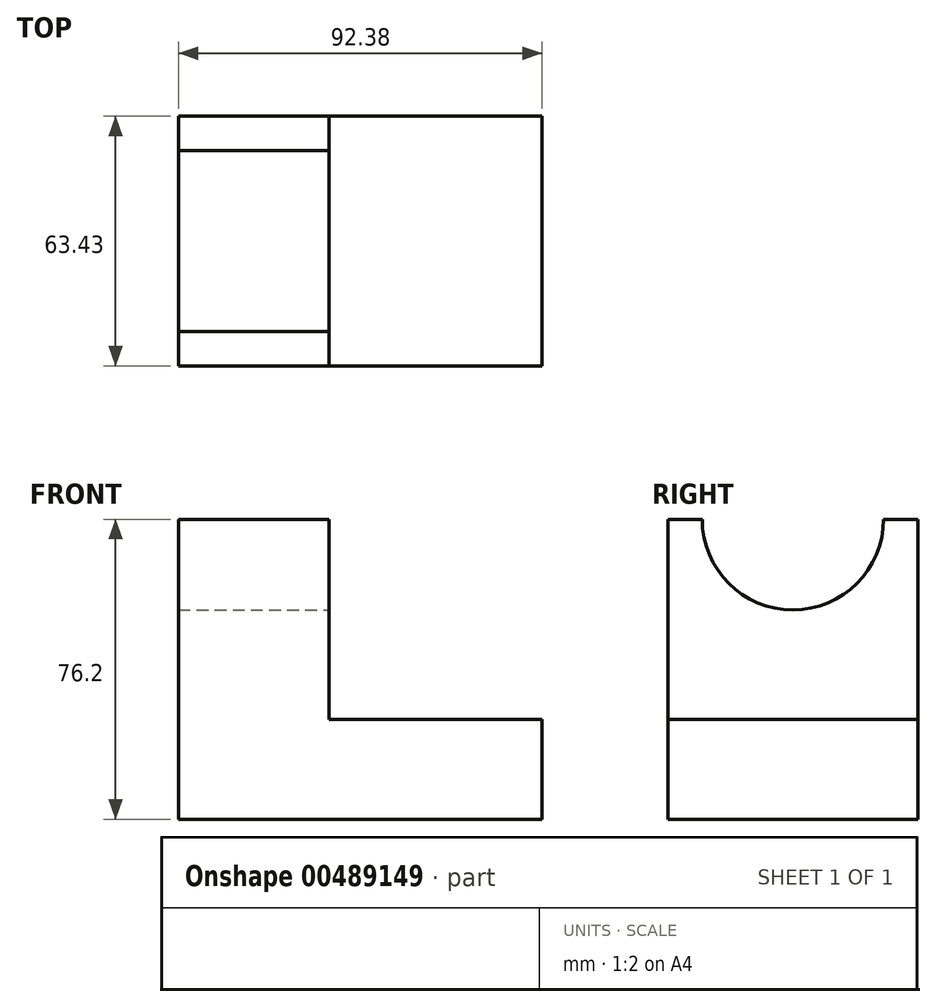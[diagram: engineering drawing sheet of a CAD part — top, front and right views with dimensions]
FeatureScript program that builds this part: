
annotation { "Feature Type Name" : "Feature", "Feature Type Description" : "" }
export const myFeature = defineFeature(function(context is Context, id is Id, definition is map)
    precondition{}
    {
        {
            var Q0;
            Q0=qCreatedBy(makeId("Top.planeOp"),FACE);
            var sketch = newSketch(context, id + "F0", { "sketchPlane" : qUnion([Q0])});
            skLineSegment(sketch, "E0.bottom", {"start": v(-46.2, 37.42) * mm, "end": v(46.19, 37.42) * mm});
            skLineSegment(sketch, "E0.top", {"start": v(-46.2, -26.01) * mm, "end": v(46.19, -26.01) * mm});
            skLineSegment(sketch, "E0.left", {"start": v(-46.2, 37.42) * mm, "end": v(-46.2, -26.01) * mm});
            skLineSegment(sketch, "E0.right", {"start": v(46.19, 37.42) * mm, "end": v(46.19, -26.01) * mm});
            skSolve(sketch);
        }
        {
            var Q0;
            Q0=makeQuery(id+"F0.imprint","IMPRINT",FACE,{"disambiguationData":[TD([[makeQuery(id+"F0.imprint","IMPRINT",EDGE,{"derivedFrom":sQuery(id+"F0.wireOp",EDGE,"E0.bottom")}),-1.0]])]});
            extrude(context, id + "F1", {"entities" : qUnion([Q0]), "depth" : 25.4 * mm});
        }
        {
            var Q0;
            Q0=makeQuery(id+"F1.opExtrude","CAP_FACE",FACE,{"disambiguationData":[OSD([sQuery(id+"F0.wireOp",EDGE,"E0.bottom"),sQuery(id+"F0.wireOp",EDGE,"E0.top"),sQuery(id+"F0.wireOp",EDGE,"E0.left"),sQuery(id+"F0.wireOp",EDGE,"E0.right")])],"isStart":false});
            var sketch = newSketch(context, id + "F2", { "sketchPlane" : qUnion([Q0])});
            skLineSegment(sketch, "E1.bottom", {"start": v(-46.2, 37.42) * mm, "end": v(-7.97, 37.42) * mm});
            skLineSegment(sketch, "E1.top", {"start": v(-46.2, -26.01) * mm, "end": v(-7.97, -26.01) * mm});
            skLineSegment(sketch, "E1.left", {"start": v(-46.2, 37.42) * mm, "end": v(-46.2, -26.01) * mm});
            skLineSegment(sketch, "E1.right", {"start": v(-7.97, 37.42) * mm, "end": v(-7.97, -26.01) * mm});
            skSolve(sketch);
        }
        {
            var Q0;
            Q0=makeQuery(id+"F2.imprint","IMPRINT",FACE,{"disambiguationData":[TD([[makeQuery(id+"F2.imprint","IMPRINT",EDGE,{"derivedFrom":sQuery(id+"F2.wireOp",EDGE,"E1.bottom")}),-1.0]])]});
            extrude(context, id + "F3", {"entities" : qUnion([Q0]), "operationType" : NewBodyOperationType.ADD, "depth" : 50.8 * mm});
        }
        {
            var Q0;
            Q0=makeQuery(id+"F1.opExtrude","CAP_FACE",FACE,{"disambiguationData":[OSD([sQuery(id+"F0.wireOp",EDGE,"E0.bottom"),sQuery(id+"F0.wireOp",EDGE,"E0.top"),sQuery(id+"F0.wireOp",EDGE,"E0.left"),sQuery(id+"F0.wireOp",EDGE,"E0.right")])],"isStart":false});
            var sketch = newSketch(context, id + "F4", { "sketchPlane" : qUnion([Q0])});
            skCircle(sketch, "E2", {"center": v(30.92, 5.7) * mm, "radius": 6.77 * mm});
            skPoint(sketch, "E2.centerSnap0", {"position": v(46.19, 5.7) * mm});
            skCircle(sketch, "E3", {"center": v(15.46, 5.7) * mm, "radius": 7.22 * mm});
            skSolve(sketch);
        }
        {
            var Q0;
            Q0=sQuery(id+"F4.wireOp",EDGE,"E3");
            var Q1;
            Q1=sQuery(id+"F4.wireOp",EDGE,"E2");
            extrude(context, id + "F5", {"bodyType" : ToolBodyType.SURFACE, "surfaceEntities" : qUnion([Q0, Q1]), "depth" : -25.4 * mm});
        }
        {
            var Q0;
            Q0=makeQuery(id+"F3.opExtrude","SWEPT_FACE",FACE,{"disambiguationData":[OSD([sQuery(id+"F2.wireOp",EDGE,"E1.right")])]});
            var sketch = newSketch(context, id + "F6", { "sketchPlane" : qUnion([Q0])});
            skCircle(sketch, "E4", {"center": v(5.7, 76.2) * mm, "radius": 23.04 * mm});
            skSolve(sketch);
        }
        {
            var Q0;
            {var subQ0=sQuery(id+"F6.wireOp",EDGE,"E4");var subQ1=makeQuery(id+"F3.opExtrude","CAP_EDGE",EDGE,{"disambiguationData":[OSD([sQuery(id+"F2.wireOp",EDGE,"E1.right")])],"isStart":false});var subQ2=makeQuery(id+"F6.imprint","INTERSECT",VERTEX,{"disambiguationData":[OD(0.0)],"derivedFrom":[subQ1,subQ0]});Q0=makeQuery(id+"F6.imprint","IMPRINT",FACE,{"disambiguationData":[TD([[makeQuery(id+"F6.imprint","IMPRINT",EDGE,{"disambiguationData":[TD([[subQ2,1.0]])],"derivedFrom":subQ0}),1.0]])]});}
            extrude(context, id + "F7", {"entities" : qUnion([Q0]), "operationType" : NewBodyOperationType.REMOVE, "oppositeDirection" : true, "depth" : 50.8 * mm});
        }
    });
